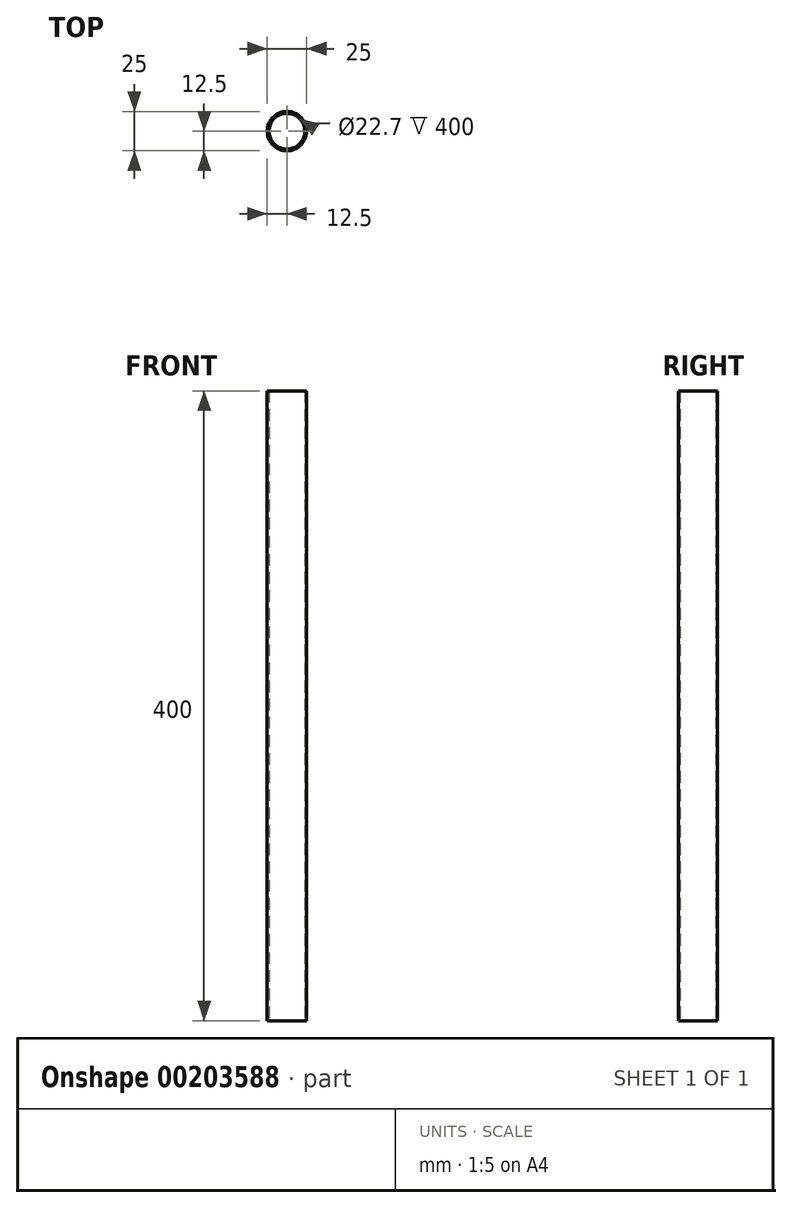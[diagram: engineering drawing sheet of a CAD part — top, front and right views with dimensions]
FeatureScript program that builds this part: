
annotation { "Feature Type Name" : "Feature", "Feature Type Description" : "" }
export const myFeature = defineFeature(function(context is Context, id is Id, definition is map)
    precondition{}
    {
        {
            var Q0;
            Q0=qCreatedBy(makeId("Top.planeOp"),FACE);
            var sketch = newSketch(context, id + "F0", { "sketchPlane" : qUnion([Q0])});
            skCircle(sketch, "E0", {"center": v(0, 0) * mm, "radius": 12.5 * mm});
            skCircle(sketch, "E1.0", {"center": v(0, 0) * mm, "radius": 11.35 * mm});
            skSolve(sketch);
        }
        {
            var Q0;
            Q0 = qSketchRegion(id + "F0", true);
            extrude(context, id + "F1", {"entities" : qUnion([Q0]), "depth" : 400 * mm});
        }
    });
